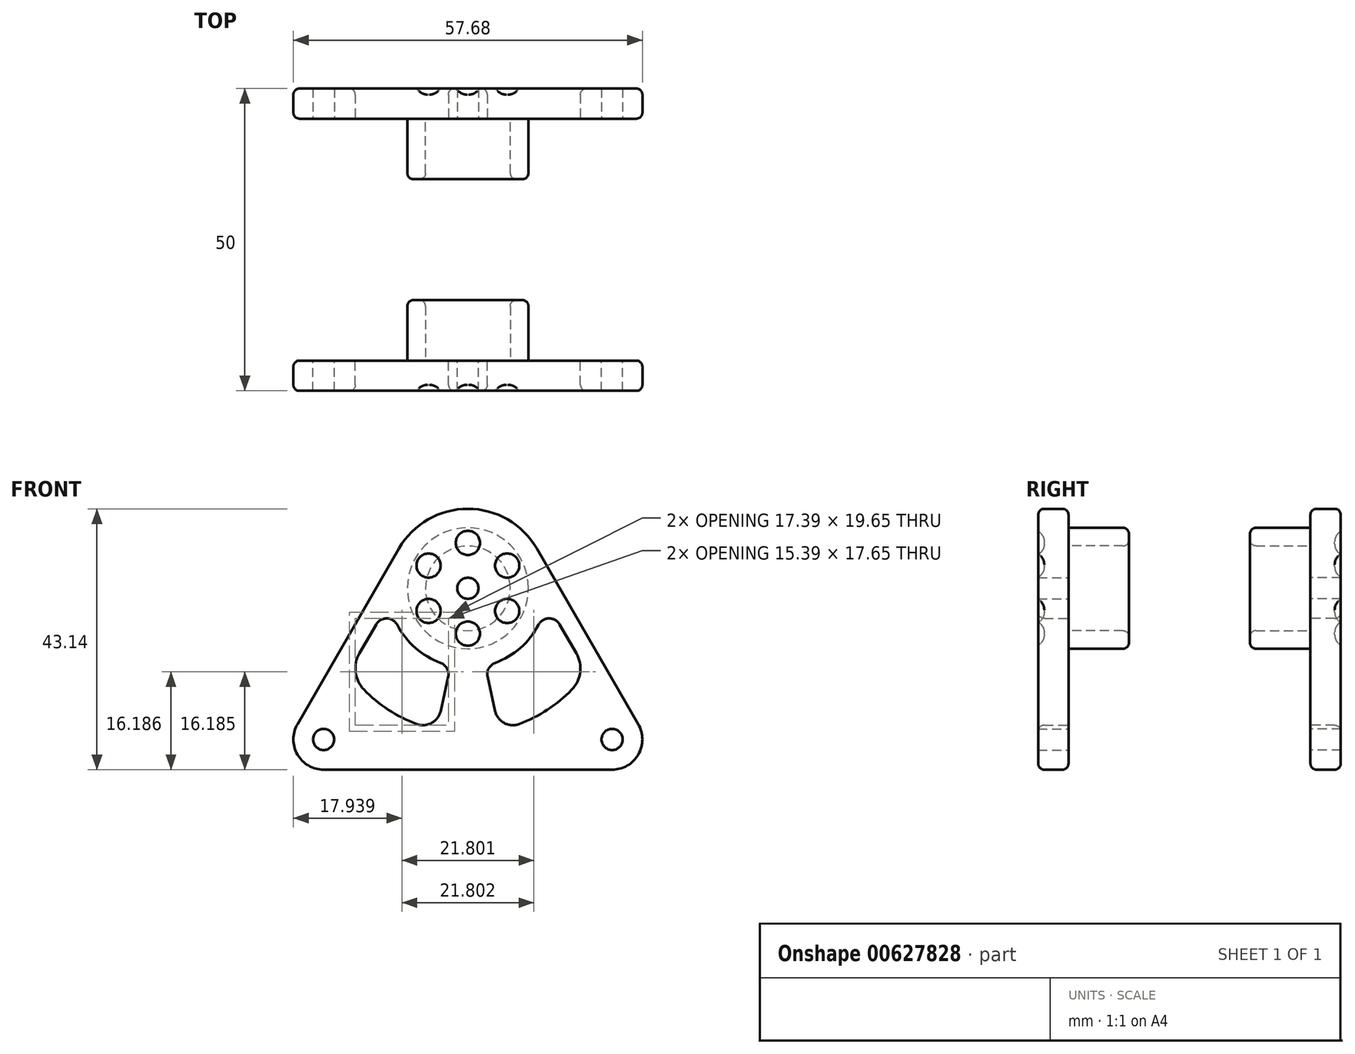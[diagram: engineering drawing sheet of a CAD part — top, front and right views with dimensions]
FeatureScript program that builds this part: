
annotation { "Feature Type Name" : "Feature", "Feature Type Description" : "" }
export const myFeature = defineFeature(function(context is Context, id is Id, definition is map)
    precondition{}
    {
        {
            var Q0;
            Q0=qCreatedBy(makeId("Front.planeOp"),FACE);
            cPlane(context, id + "F0", {"entities" : qUnion([Q0]), "cplaneType" : CPlaneType.OFFSET, "offset" : 20 * mm, "oppositeDirection" : true, "width" : 150 * mm, "height" : 150 * mm});
        }
        {
            var Q0;
            Q0=qCreatedBy(makeId("Front.planeOp"),FACE);
            var sketch = newSketch(context, id + "F1", { "sketchPlane" : qUnion([Q0])});
            skLineSegment(sketch, "E0", {"start": v(0, 37.53) * mm, "end": v(-32.5, -18.76) * mm});
            skLineSegment(sketch, "E1", {"start": v(-32.5, -18.76) * mm, "end": v(32.5, -18.76) * mm});
            skLineSegment(sketch, "E2", {"start": v(32.5, -18.76) * mm, "end": v(0, 37.53) * mm});
            skLineSegment(sketch, "E3", {"start": v(0, 37.53) * mm, "end": v(0, -18.76) * mm, "construction": true});
            skLineSegment(sketch, "E4", {"start": v(32.5, -18.76) * mm, "end": v(-16.25, 9.38) * mm, "construction": true});
            skCircle(sketch, "E5", {"center": v(0, 11.24) * mm, "radius": 25 * mm, "construction": true});
            skCircle(sketch, "E6", {"center": v(0, 11.24) * mm, "radius": 10 * mm, "construction": true});
            skSolve(sketch);
        }
        {
            var Q0;
            Q0 = qSketchRegion(id + "F1", true);
            extrude(context, id + "F2", {"entities" : qUnion([Q0]), "depth" : 5 * mm, "offsetDistance" : 25 * mm});
        }
        {
            var Q0;
            Q0=makeQuery(id+"F1.imprint","IMPRINT",FACE,{"disambiguationData":[TD([[makeQuery(id+"F1.imprint","IMPRINT",EDGE,{"derivedFrom":sQuery(id+"F1.wireOp",EDGE,"E0")}),1.0]])]});
            var sketch = newSketch(context, id + "F3", { "sketchPlane" : qUnion([Q0])});
            skCircle(sketch, "E7", {"center": v(0, 11.24) * mm, "radius": 10 * mm});
            skCircle(sketch, "E8", {"center": v(0, 11.24) * mm, "radius": 7 * mm});
            skSolve(sketch);
        }
        {
            var Q0;
            Q0 = qSketchRegion(id + "F3", true);
            extrude(context, id + "F4", {"entities" : qUnion([Q0]), "operationType" : NewBodyOperationType.ADD, "oppositeDirection" : true, "depth" : 10 * mm, "offsetDistance" : 25 * mm});
        }
        {
            var Q0;
            Q0=makeQuery(id+"F1.imprint","IMPRINT",FACE,{"disambiguationData":[TD([[makeQuery(id+"F1.imprint","IMPRINT",EDGE,{"derivedFrom":sQuery(id+"F1.wireOp",EDGE,"E0")}),1.0]])]});
            var sketch = newSketch(context, id + "F5", { "sketchPlane" : qUnion([Q0])});
            skArc(sketch, "E9", {"start": v(11.38, 17.8) * mm, "mid": v(0, 24.38) * mm, "end": v(-11.38, 17.8) * mm});
            skLineSegment(sketch, "E10.0", {"start": v(11.38, 17.8) * mm, "end": v(0, 37.53) * mm});
            skLineSegment(sketch, "E11.0", {"start": v(0, 37.53) * mm, "end": v(-11.38, 17.8) * mm});
            skPoint(sketch, "E12.orphan", {"position": v(32.5, -18.76) * mm});
            skPoint(sketch, "E13.orphan", {"position": v(-32.5, -18.76) * mm});
            skSolve(sketch);
        }
        {
            var Q0;
            Q0 = qSketchRegion(id + "F5", true);
            extrude(context, id + "F6", {"entities" : qUnion([Q0]), "operationType" : NewBodyOperationType.REMOVE, "endBound" : BoundingType.THROUGH_ALL, "depth" : 25 * mm, "offsetDistance" : 25 * mm});
        }
        {
            var Q0;
            Q0=makeQuery(id+"F2.opExtrude","SWEPT_EDGE",EDGE,{"disambiguationData":[OSD([sQuery(id+"F1.wireOp",EDGE,"E1"),sQuery(id+"F1.wireOp",EDGE,"E2")])]});
            var Q1;
            Q1=makeQuery(id+"F2.opExtrude","SWEPT_EDGE",EDGE,{"disambiguationData":[OSD([sQuery(id+"F1.wireOp",EDGE,"E0"),sQuery(id+"F1.wireOp",EDGE,"E1")])]});
            fillet(context, id + "F7", {"entities" : qUnion([Q0, Q1]), "radius" : 5 * mm, "tangentPropagation" : true, "allowEdgeOverflow" : false});
        }
        {
            var Q0;
            Q0=makeQuery(id+"F1.imprint","IMPRINT",FACE,{"disambiguationData":[TD([[makeQuery(id+"F1.imprint","IMPRINT",EDGE,{"derivedFrom":sQuery(id+"F1.wireOp",EDGE,"E0")}),1.0]])]});
            var sketch = newSketch(context, id + "F8", { "sketchPlane" : qUnion([Q0])});
            skCircle(sketch, "E14", {"center": v(23.84, -13.76) * mm, "radius": 1.75 * mm});
            skCircle(sketch, "E15", {"center": v(-23.84, -13.76) * mm, "radius": 1.75 * mm});
            skCircle(sketch, "E16", {"center": v(0, 11.24) * mm, "radius": 1.75 * mm});
            skSolve(sketch);
        }
        {
            var Q0;
            Q0 = qSketchRegion(id + "F8", true);
            extrude(context, id + "F9", {"entities" : qUnion([Q0]), "operationType" : NewBodyOperationType.REMOVE, "endBound" : BoundingType.THROUGH_ALL, "depth" : 25 * mm, "offsetDistance" : 25 * mm});
        }
        {
            var Q0;
            Q0=makeQuery(id+"F1.imprint","IMPRINT",FACE,{"disambiguationData":[TD([[makeQuery(id+"F1.imprint","IMPRINT",EDGE,{"derivedFrom":sQuery(id+"F1.wireOp",EDGE,"E0")}),1.0]])]});
            var sketch = newSketch(context, id + "F10", { "sketchPlane" : qUnion([Q0])});
            skArc(sketch, "E17", {"start": v(-19.66, -2.53) * mm, "mid": v(-13.34, -8.72) * mm, "end": v(-5.2, -12.2) * mm});
            skArc(sketch, "E18", {"start": v(-12.97, 9.07) * mm, "mid": v(-9.54, 2.19) * mm, "end": v(-2.85, -1.6) * mm});
            skLineSegment(sketch, "E19", {"start": v(12.97, 9.07) * mm, "end": v(19.66, -2.53) * mm});
            skLineSegment(sketch, "E20", {"start": v(-12.97, 9.07) * mm, "end": v(-19.66, -2.53) * mm});
            skLineSegment(sketch, "E21", {"start": v(2.85, -1.6) * mm, "end": v(5.2, -12.2) * mm});
            skLineSegment(sketch, "E22", {"start": v(-2.85, -1.6) * mm, "end": v(-5.2, -12.2) * mm});
            skArc(sketch, "E23.trimOffspring", {"start": v(2.85, -1.6) * mm, "mid": v(9.54, 2.19) * mm, "end": v(12.97, 9.07) * mm});
            skArc(sketch, "E24.trimOffspring", {"start": v(5.2, -12.2) * mm, "mid": v(13.34, -8.72) * mm, "end": v(19.66, -2.53) * mm});
            skLineSegment(sketch, "E25", {"start": v(0, 11.24) * mm, "end": v(0, -14.43) * mm, "construction": true});
            skSolve(sketch);
        }
        {
            var Q0;
            Q0 = qSketchRegion(id + "F10", true);
            extrude(context, id + "F11", {"entities" : qUnion([Q0]), "operationType" : NewBodyOperationType.REMOVE, "endBound" : BoundingType.THROUGH_ALL, "depth" : 25 * mm, "offsetDistance" : 25 * mm});
        }
        {
            var Q0;
            Q0=makeQuery(id+"F11.boolean.opBoolean","COPY",EDGE,{"derivedFrom":makeQuery(id+"F11.opExtrude","SWEPT_EDGE",EDGE,{"disambiguationData":[OSD([sQuery(id+"F10.wireOp",EDGE,"E19"),sQuery(id+"F10.wireOp",EDGE,"E23.trimOffspring")])]})});
            var Q1;
            Q1=makeQuery(id+"F11.boolean.opBoolean","COPY",EDGE,{"derivedFrom":makeQuery(id+"F11.opExtrude","SWEPT_EDGE",EDGE,{"disambiguationData":[OSD([sQuery(id+"F10.wireOp",EDGE,"E18"),sQuery(id+"F10.wireOp",EDGE,"E20")])]})});
            var Q2;
            Q2=makeQuery(id+"F11.boolean.opBoolean","COPY",EDGE,{"derivedFrom":makeQuery(id+"F11.opExtrude","SWEPT_EDGE",EDGE,{"disambiguationData":[OSD([sQuery(id+"F10.wireOp",EDGE,"E18"),sQuery(id+"F10.wireOp",EDGE,"E22")])]})});
            var Q3;
            Q3=makeQuery(id+"F11.boolean.opBoolean","COPY",EDGE,{"derivedFrom":makeQuery(id+"F11.opExtrude","SWEPT_EDGE",EDGE,{"disambiguationData":[OSD([sQuery(id+"F10.wireOp",EDGE,"E21"),sQuery(id+"F10.wireOp",EDGE,"E23.trimOffspring")])]})});
            fillet(context, id + "F12", {"entities" : qUnion([Q0, Q1, Q2, Q3]), "radius" : 2 * mm, "tangentPropagation" : true, "allowEdgeOverflow" : false});
        }
        {
            var Q0;
            Q0=makeQuery(id+"F11.boolean.opBoolean","COPY",EDGE,{"derivedFrom":makeQuery(id+"F11.opExtrude","SWEPT_EDGE",EDGE,{"disambiguationData":[OSD([sQuery(id+"F10.wireOp",EDGE,"E19"),sQuery(id+"F10.wireOp",EDGE,"E24.trimOffspring")])]})});
            var Q1;
            Q1=makeQuery(id+"F11.boolean.opBoolean","COPY",EDGE,{"derivedFrom":makeQuery(id+"F11.opExtrude","SWEPT_EDGE",EDGE,{"disambiguationData":[OSD([sQuery(id+"F10.wireOp",EDGE,"E17"),sQuery(id+"F10.wireOp",EDGE,"E20")])]})});
            fillet(context, id + "F13", {"entities" : qUnion([Q0, Q1]), "radius" : 5 * mm, "tangentPropagation" : true, "allowEdgeOverflow" : false});
        }
        {
            var Q0;
            Q0=makeQuery(id+"F11.boolean.opBoolean","COPY",EDGE,{"derivedFrom":makeQuery(id+"F11.opExtrude","SWEPT_EDGE",EDGE,{"disambiguationData":[OSD([sQuery(id+"F10.wireOp",EDGE,"E21"),sQuery(id+"F10.wireOp",EDGE,"E24.trimOffspring")])]})});
            var Q1;
            Q1=makeQuery(id+"F11.boolean.opBoolean","COPY",EDGE,{"derivedFrom":makeQuery(id+"F11.opExtrude","SWEPT_EDGE",EDGE,{"disambiguationData":[OSD([sQuery(id+"F10.wireOp",EDGE,"E17"),sQuery(id+"F10.wireOp",EDGE,"E22")])]})});
            fillet(context, id + "F14", {"entities" : qUnion([Q0, Q1]), "radius" : 3 * mm, "tangentPropagation" : true, "allowEdgeOverflow" : false});
        }
        {
            var Q0;
            Q0=makeQuery(id+"F2.opExtrude","CAP_EDGE",EDGE,{"disambiguationData":[OSD([sQuery(id+"F1.wireOp",EDGE,"E0")])],"isStart":false});
            var Q1;
            Q1=makeQuery(id+"F12.opFillet","BLEND_EDGE",EDGE,{"blendedFrom":[makeQuery(id+"F11.boolean.opBoolean","COPY",EDGE,{"derivedFrom":makeQuery(id+"F11.opExtrude","SWEPT_EDGE",EDGE,{"disambiguationData":[OSD([sQuery(id+"F10.wireOp",EDGE,"E18"),sQuery(id+"F10.wireOp",EDGE,"E20")])]})}),makeQuery(id+"F2.opExtrude","CAP_FACE",FACE,{"disambiguationData":[OSD([sQuery(id+"F1.wireOp",EDGE,"E0"),sQuery(id+"F1.wireOp",EDGE,"E1"),sQuery(id+"F1.wireOp",EDGE,"E2")])],"isStart":false})],"blendedInto":[makeQuery(id+"F2.opExtrude","CAP_FACE",FACE,{"disambiguationData":[OSD([sQuery(id+"F1.wireOp",EDGE,"E0"),sQuery(id+"F1.wireOp",EDGE,"E1"),sQuery(id+"F1.wireOp",EDGE,"E2")])],"isStart":false})]});
            var Q2;
            Q2=makeQuery(id+"F12.opFillet","BLEND_EDGE",EDGE,{"blendedFrom":[makeQuery(id+"F11.boolean.opBoolean","COPY",EDGE,{"derivedFrom":makeQuery(id+"F11.opExtrude","SWEPT_EDGE",EDGE,{"disambiguationData":[OSD([sQuery(id+"F10.wireOp",EDGE,"E19"),sQuery(id+"F10.wireOp",EDGE,"E23.trimOffspring")])]})}),makeQuery(id+"F2.opExtrude","CAP_FACE",FACE,{"disambiguationData":[OSD([sQuery(id+"F1.wireOp",EDGE,"E0"),sQuery(id+"F1.wireOp",EDGE,"E1"),sQuery(id+"F1.wireOp",EDGE,"E2")])],"isStart":false})],"blendedInto":[makeQuery(id+"F2.opExtrude","CAP_FACE",FACE,{"disambiguationData":[OSD([sQuery(id+"F1.wireOp",EDGE,"E0"),sQuery(id+"F1.wireOp",EDGE,"E1"),sQuery(id+"F1.wireOp",EDGE,"E2")])],"isStart":false})]});
            var Q3;
            Q3=makeQuery(id+"F2.opExtrude","CAP_EDGE",EDGE,{"disambiguationData":[OSD([sQuery(id+"F1.wireOp",EDGE,"E2")])],"isStart":true});
            var Q4;
            Q4=makeQuery(id+"F11.boolean.opBoolean","COPY",EDGE,{"derivedFrom":makeQuery(id+"F11.opExtrude","CAP_EDGE",EDGE,{"disambiguationData":[OSD([sQuery(id+"F10.wireOp",EDGE,"E23.trimOffspring")])],"isStart":true})});
            var Q5;
            Q5=makeQuery(id+"F11.boolean.opBoolean","COPY",EDGE,{"derivedFrom":makeQuery(id+"F11.opExtrude","CAP_EDGE",EDGE,{"disambiguationData":[OSD([sQuery(id+"F10.wireOp",EDGE,"E18")])],"isStart":true})});
            fillet(context, id + "F15", {"entities" : qUnion([Q0, Q1, Q2, Q3, Q4, Q5]), "radius" : 1 * mm, "tangentPropagation" : true, "allowEdgeOverflow" : false});
        }
        {
            var Q0;
            Q0=makeQuery(id+"F4.opExtrude","CAP_EDGE",EDGE,{"disambiguationData":[OSD([sQuery(id+"F3.wireOp",EDGE,"E8")])],"isStart":true});
            var Q1;
            Q1=makeQuery(id+"F4.opExtrude","CAP_FACE",FACE,{"disambiguationData":[OSD([sQuery(id+"F3.wireOp",EDGE,"E7"),sQuery(id+"F3.wireOp",EDGE,"E8")])],"isStart":false});
            fillet(context, id + "F16", {"entities" : qUnion([Q0, Q1]), "radius" : 1 * mm, "tangentPropagation" : true, "allowEdgeOverflow" : false});
        }
        {
            var Q0;
            Q0=makeQuery(id+"F2.opExtrude","CAP_FACE",FACE,{"disambiguationData":[OSD([sQuery(id+"F1.wireOp",EDGE,"E0"),sQuery(id+"F1.wireOp",EDGE,"E1"),sQuery(id+"F1.wireOp",EDGE,"E2")])],"isStart":false});
            var sketch = newSketch(context, id + "F17", { "sketchPlane" : qUnion([Q0])});
            skCircle(sketch, "E26", {"center": v(0, 11.24) * mm, "radius": 7.5 * mm, "construction": true});
            skCircle(sketch, "E27", {"center": v(0, 18.74) * mm, "radius": 2 * mm});
            skCircle(sketch, "E28.1.0", {"center": v(-6.5, 14.99) * mm, "radius": 2 * mm});
            skCircle(sketch, "E28.2.0", {"center": v(-6.5, 7.49) * mm, "radius": 2 * mm});
            skCircle(sketch, "E28.3.0", {"center": v(0, 3.74) * mm, "radius": 2 * mm});
            skCircle(sketch, "E28.4.0", {"center": v(6.5, 7.49) * mm, "radius": 2 * mm});
            skCircle(sketch, "E28.5.0", {"center": v(6.5, 14.99) * mm, "radius": 2 * mm});
            skSolve(sketch);
        }
        {
            var Q0;
            Q0 = qSketchRegion(id + "F17", true);
            extrude(context, id + "F18", {"entities" : qUnion([Q0]), "operationType" : NewBodyOperationType.REMOVE, "oppositeDirection" : true, "depth" : 1 * mm, "offsetDistance" : 25 * mm, "hasDraft" : true, "draftAngle" : 45 * degree, "draftPullDirection" : true});
        }
        {
            var Q0;
            Q0=makeQuery(id+"F18.boolean.opBoolean","COPY",FACE,{"derivedFrom":makeQuery(id+"F18.opExtrude","CAP_FACE",FACE,{"disambiguationData":[OSD([sQuery(id+"F17.wireOp",EDGE,"E28.1.0")])],"isStart":false})});
            var Q1;
            Q1=makeQuery(id+"F18.boolean.opBoolean","COPY",FACE,{"derivedFrom":makeQuery(id+"F18.opExtrude","CAP_FACE",FACE,{"disambiguationData":[OSD([sQuery(id+"F17.wireOp",EDGE,"E28.2.0")])],"isStart":false})});
            var Q2;
            Q2=makeQuery(id+"F18.boolean.opBoolean","COPY",FACE,{"derivedFrom":makeQuery(id+"F18.opExtrude","CAP_FACE",FACE,{"disambiguationData":[OSD([sQuery(id+"F17.wireOp",EDGE,"E28.3.0")])],"isStart":false})});
            var Q3;
            Q3=makeQuery(id+"F18.boolean.opBoolean","COPY",FACE,{"derivedFrom":makeQuery(id+"F18.opExtrude","CAP_FACE",FACE,{"disambiguationData":[OSD([sQuery(id+"F17.wireOp",EDGE,"E28.4.0")])],"isStart":false})});
            var Q4;
            Q4=makeQuery(id+"F18.boolean.opBoolean","COPY",FACE,{"derivedFrom":makeQuery(id+"F18.opExtrude","CAP_FACE",FACE,{"disambiguationData":[OSD([sQuery(id+"F17.wireOp",EDGE,"E28.5.0")])],"isStart":false})});
            var Q5;
            Q5=makeQuery(id+"F18.boolean.opBoolean","COPY",FACE,{"derivedFrom":makeQuery(id+"F18.opExtrude","CAP_FACE",FACE,{"disambiguationData":[OSD([sQuery(id+"F17.wireOp",EDGE,"E27")])],"isStart":false})});
            fillet(context, id + "F19", {"entities" : qUnion([Q0, Q1, Q2, Q3, Q4, Q5]), "radius" : 2 * mm, "tangentPropagation" : true, "allowEdgeOverflow" : false});
        }
        {
            var Q0;
            Q0=makeQuery(id+"F2.opExtrude","SWEPT_BODY",BODY,{"disambiguationData":[OSD([sQuery(id+"F1.wireOp",EDGE,"E0"),sQuery(id+"F1.wireOp",EDGE,"E1"),sQuery(id+"F1.wireOp",EDGE,"E2")])]});
            var Q1;
            Q1=qCreatedBy(id+"F0.planeOp",FACE);
            mirror(context, id + "F20", {"entities" : qUnion([Q0]), "mirrorPlane" : qUnion([Q1])});
        }
    });
